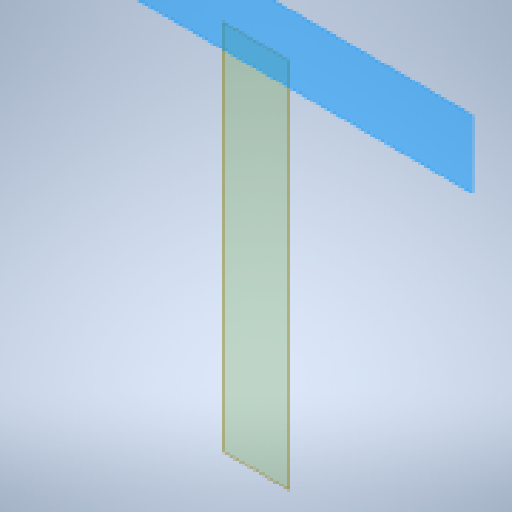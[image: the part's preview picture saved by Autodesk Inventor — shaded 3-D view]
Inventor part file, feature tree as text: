
AUTODESK INVENTOR PART (.ipt)
format: ipt  version: 2024.1 (Build 281209000, 209)  size: 120,320 bytes
history: native  units: mm
features: other x3, plane x1
ambient origin geometry x8: Origin, YZ Plane, XZ Plane, XY Plane, X Axis, Y Axis, Z Axis, Center Point
feature tree (4):
  plane  "Work Plane1"
  other  "<userpath>\Documents\0004-CAD\3D-cad-main\the-artifact\artifact-assembly.iam"
  other  "artifact-assembly.iam"
  other  "see-saw-arm:1"
